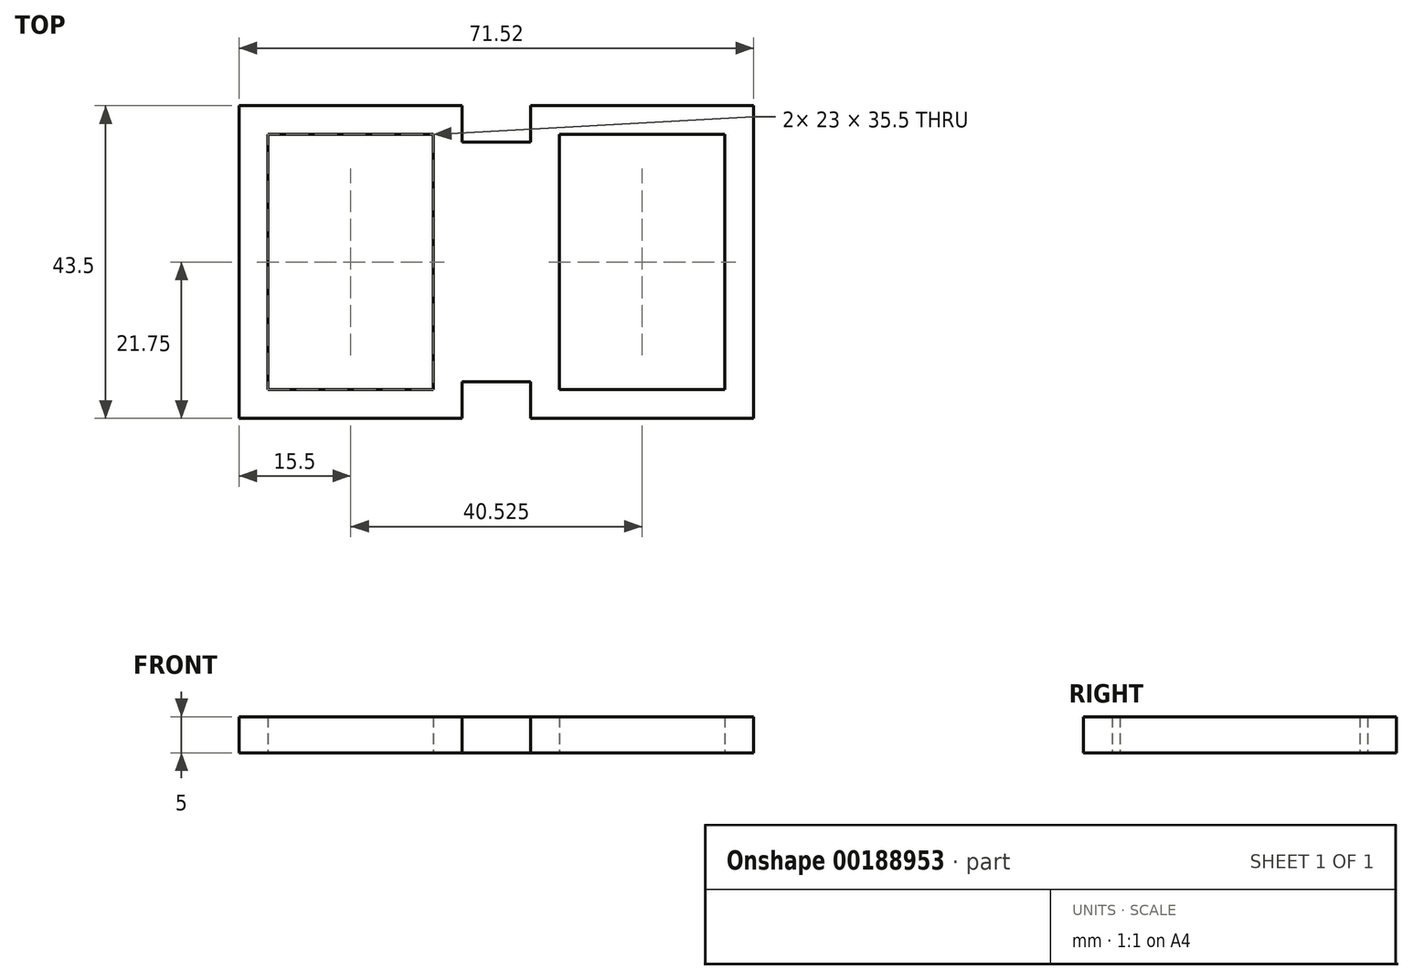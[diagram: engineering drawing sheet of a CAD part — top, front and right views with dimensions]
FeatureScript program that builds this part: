
annotation { "Feature Type Name" : "Feature", "Feature Type Description" : "" }
export const myFeature = defineFeature(function(context is Context, id is Id, definition is map)
    precondition{}
    {
        {
            var Q0;
            Q0=qCreatedBy(makeId("Top.planeOp"),FACE);
            var sketch = newSketch(context, id + "F0", { "sketchPlane" : qUnion([Q0])});
            skLineSegment(sketch, "E0.bottom", {"start": v(0, 0) * mm, "end": v(-31, 0) * mm});
            skLineSegment(sketch, "E0.top", {"start": v(0, 43.5) * mm, "end": v(-31, 43.5) * mm});
            skLineSegment(sketch, "E0.left", {"start": v(0, 0) * mm, "end": v(0, 43.5) * mm});
            skLineSegment(sketch, "E0.right", {"start": v(-31, 0) * mm, "end": v(-31, 43.5) * mm});
            skLineSegment(sketch, "E1.bottom", {"start": v(-27, 39.5) * mm, "end": v(-4, 39.5) * mm});
            skLineSegment(sketch, "E1.top", {"start": v(-27, 4) * mm, "end": v(-4, 4) * mm});
            skLineSegment(sketch, "E1.left", {"start": v(-27, 39.5) * mm, "end": v(-27, 4) * mm});
            skLineSegment(sketch, "E1.right", {"start": v(-4, 39.5) * mm, "end": v(-4, 4) * mm});
            skLineSegment(sketch, "E2.bottom", {"start": v(9.52, 43.5) * mm, "end": v(40.52, 43.5) * mm});
            skLineSegment(sketch, "E2.top", {"start": v(9.52, 0) * mm, "end": v(40.52, 0) * mm});
            skLineSegment(sketch, "E2.left", {"start": v(9.52, 43.5) * mm, "end": v(9.52, 0) * mm});
            skLineSegment(sketch, "E2.right", {"start": v(40.52, 43.5) * mm, "end": v(40.52, 0) * mm});
            skLineSegment(sketch, "E3.bottom", {"start": v(13.52, 39.5) * mm, "end": v(36.52, 39.5) * mm});
            skLineSegment(sketch, "E3.top", {"start": v(13.52, 4) * mm, "end": v(36.52, 4) * mm});
            skLineSegment(sketch, "E3.left", {"start": v(13.52, 39.5) * mm, "end": v(13.52, 4) * mm});
            skLineSegment(sketch, "E3.right", {"start": v(36.52, 39.5) * mm, "end": v(36.52, 4) * mm});
            skLineSegment(sketch, "E4.bottom", {"start": v(0, 38.42) * mm, "end": v(9.52, 38.42) * mm});
            skLineSegment(sketch, "E4.top", {"start": v(0, 5.08) * mm, "end": v(9.52, 5.08) * mm});
            skLineSegment(sketch, "E4.left", {"start": v(0, 38.42) * mm, "end": v(0, 5.08) * mm});
            skLineSegment(sketch, "E4.right", {"start": v(9.52, 38.42) * mm, "end": v(9.52, 5.08) * mm});
            skSolve(sketch);
        }
        {
            var Q0;
            Q0=makeQuery(id+"F0.imprint","IMPRINT",FACE,{"disambiguationData":[TD([[makeQuery(id+"F0.imprint","IMPRINT",EDGE,{"derivedFrom":sQuery(id+"F0.wireOp",EDGE,"E0.bottom")}),-1.0]])]});
            var Q1;
            Q1=makeQuery(id+"F0.imprint","IMPRINT",FACE,{"disambiguationData":[TD([[makeQuery(id+"F0.imprint","IMPRINT",EDGE,{"derivedFrom":sQuery(id+"F0.wireOp",EDGE,"E4.bottom")}),-1.0]])]});
            var Q2;
            {var subQ3=sQuery(id+"F0.wireOp",EDGE,"E2.bottom");Q2=makeQuery(id+"F0.imprint","IMPRINT",FACE,{"disambiguationData":[TD([[makeQuery(id+"F0.imprint","IMPRINT",EDGE,{"derivedFrom":subQ3}),-1.0]])]});}
            extrude(context, id + "F1", {"entities" : qUnion([Q0, Q1, Q2]), "depth" : 5 * mm});
        }
    });
